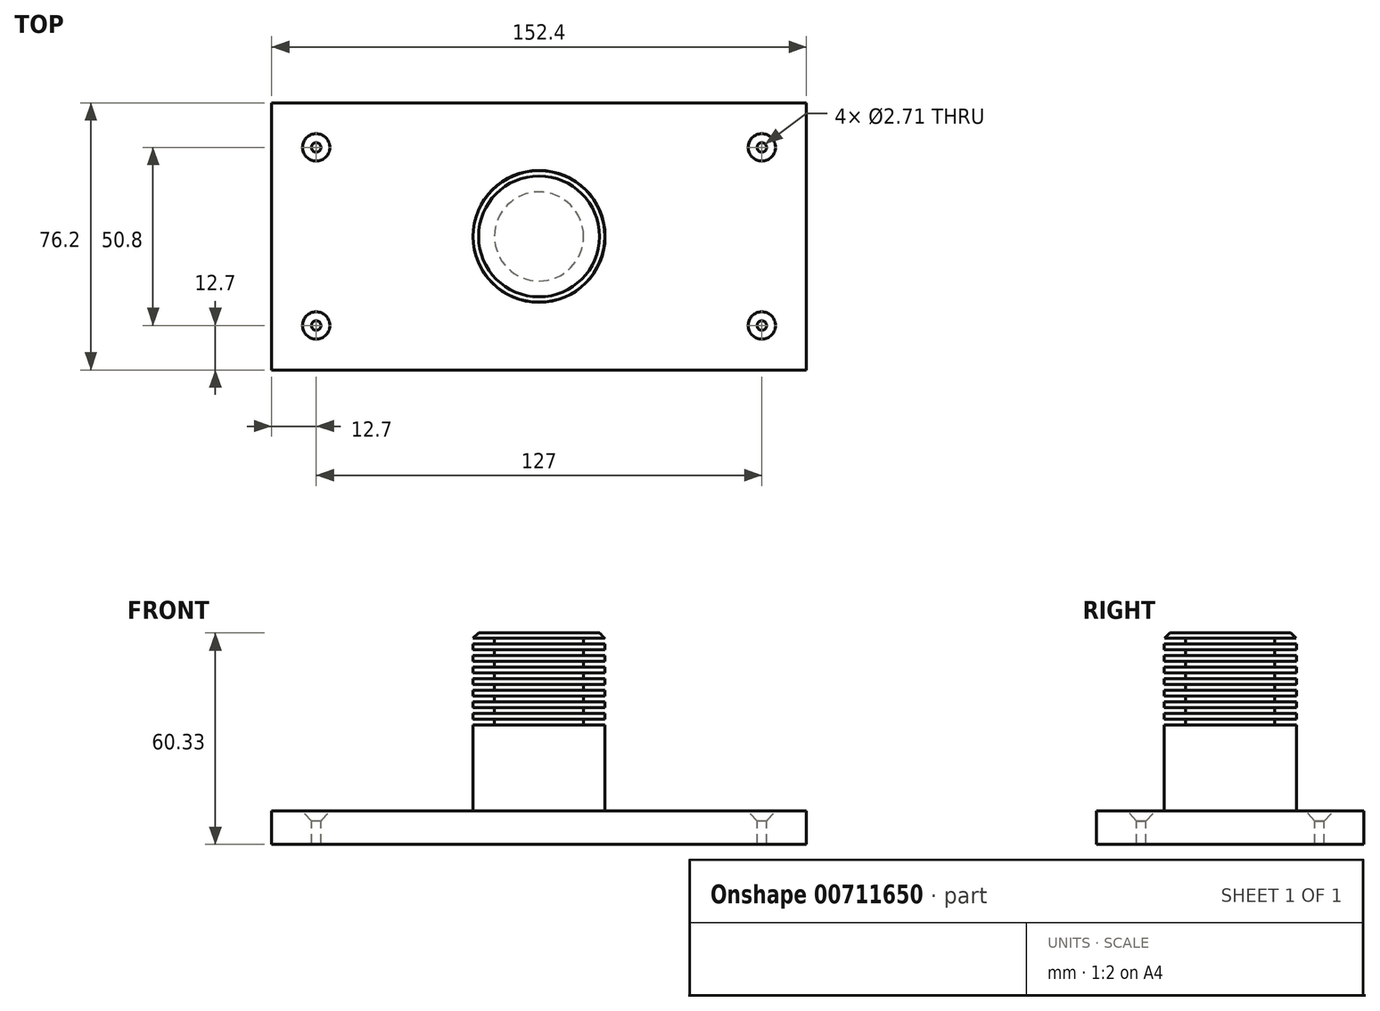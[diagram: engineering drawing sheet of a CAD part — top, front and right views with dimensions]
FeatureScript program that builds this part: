
annotation { "Feature Type Name" : "Feature", "Feature Type Description" : "" }
export const myFeature = defineFeature(function(context is Context, id is Id, definition is map)
    precondition{}
    {
        {
            var Q0;
            Q0=qCreatedBy(makeId("Top.planeOp"),FACE);
            var sketch = newSketch(context, id + "F0", { "sketchPlane" : qUnion([Q0])});
            skLineSegment(sketch, "E0.bottom", {"start": v(-76.2, 38.1) * mm, "end": v(76.2, 38.1) * mm});
            skLineSegment(sketch, "E0.top", {"start": v(-76.2, -38.1) * mm, "end": v(76.2, -38.1) * mm});
            skLineSegment(sketch, "E0.left", {"start": v(-76.2, 38.1) * mm, "end": v(-76.2, -38.1) * mm});
            skLineSegment(sketch, "E0.right", {"start": v(76.2, 38.1) * mm, "end": v(76.2, -38.1) * mm});
            skPoint(sketch, "E0.middle", {"position": v(0, 0) * mm});
            skSolve(sketch);
        }
        {
            var Q0;
            Q0=makeQuery(id+"F0.imprint","IMPRINT",FACE,{"disambiguationData":[TD([[makeQuery(id+"F0.imprint","IMPRINT",EDGE,{"derivedFrom":sQuery(id+"F0.wireOp",EDGE,"E0.bottom")}),-1.0]])]});
            extrude(context, id + "F1", {"entities" : qUnion([Q0]), "depth" : 9.52 * mm, "offsetDistance" : 25.4 * mm});
        }
        {
            var Q0;
            Q0=makeQuery(id+"F1.opExtrude","CAP_FACE",FACE,{"disambiguationData":[OSD([sQuery(id+"F0.wireOp",EDGE,"E0.bottom"),sQuery(id+"F0.wireOp",EDGE,"E0.top"),sQuery(id+"F0.wireOp",EDGE,"E0.left"),sQuery(id+"F0.wireOp",EDGE,"E0.right")])],"isStart":false});
            var sketch = newSketch(context, id + "F2", { "sketchPlane" : qUnion([Q0])});
            skPoint(sketch, "E1", {"position": v(-63.5, 25.4) * mm});
            skPoint(sketch, "E2", {"position": v(63.5, 25.4) * mm});
            skPoint(sketch, "E3.MirrorP", {"position": v(-63.5, -25.4) * mm});
            skPoint(sketch, "E4.MirrorP", {"position": v(63.5, -25.4) * mm});
            skSolve(sketch);
        }
        {
            var Q0;
            Q0=sQuery(id+"F2.wireOp",VERTEX,"E1");
            var Q1;
            Q1=sQuery(id+"F2.wireOp",VERTEX,"E2");
            var Q2;
            Q2=sQuery(id+"F2.wireOp",VERTEX,"E3.MirrorP");
            var Q3;
            Q3=sQuery(id+"F2.wireOp",VERTEX,"E4.MirrorP");
            var Q4;
            Q4=makeQuery(id+"F1.opExtrude","SWEPT_BODY",BODY,{"disambiguationData":[OSD([sQuery(id+"F0.wireOp",EDGE,"E0.bottom"),sQuery(id+"F0.wireOp",EDGE,"E0.top"),sQuery(id+"F0.wireOp",EDGE,"E0.left"),sQuery(id+"F0.wireOp",EDGE,"E0.right")])]});
            hole(context, id + "F3", {"style" : HoleStyle.C_SINK, "endStyle" : HoleEndStyle.THROUGH, "standardTappedOrClearance" : lookupTablePath({ "standard" : "ANSI", "engagement" : "75%", "pitch" : "32 tpi", "size" : "#6", "type" : "Tapped" }), "standardBlindInLast" : lookupTablePath({ "standard" : "ANSI", "engagement" : "75%", "pitch" : "32 tpi", "size" : "#6", "type" : "Tapped" }), "holeDiameter" : 2.7 * mm, "cSinkDiameter" : 7.8 * mm, "cSinkAngle" : 82 * degree, "majorDiameter" : 3.5 * mm, "showTappedDepth" : true, "isTappedThrough" : true, "tappedDepth" : 12.7 * mm, "tapClearance" : 3, "startFromSketch" : true, "locations" : qUnion([Q0, Q1, Q2, Q3]), "scope" : qUnion([Q4])});
        }
        {
            var Q0;
            Q0=makeQuery(id+"F1.opExtrude","CAP_FACE",FACE,{"disambiguationData":[OSD([sQuery(id+"F0.wireOp",EDGE,"E0.bottom"),sQuery(id+"F0.wireOp",EDGE,"E0.top"),sQuery(id+"F0.wireOp",EDGE,"E0.left"),sQuery(id+"F0.wireOp",EDGE,"E0.right")])],"isStart":false});
            var sketch = newSketch(context, id + "F4", { "sketchPlane" : qUnion([Q0])});
            skCircle(sketch, "E5", {"center": v(0, 0) * mm, "radius": 18.82 * mm});
            skSolve(sketch);
        }
        {
            var Q0;
            Q0 = qSketchRegion(id + "F4", true);
            extrude(context, id + "F5", {"entities" : qUnion([Q0]), "operationType" : NewBodyOperationType.ADD, "depth" : 50.8 * mm, "offsetDistance" : 25.4 * mm});
        }
        {
            var Q0;
            Q0=qCreatedBy(makeId("Front.planeOp"),FACE);
            var sketch = newSketch(context, id + "F6", { "sketchPlane" : qUnion([Q0])});
            skLineSegment(sketch, "E6.bottom", {"start": v(27.04, 35.68) * mm, "end": v(12.7, 35.68) * mm});
            skLineSegment(sketch, "E6.top", {"start": v(27.04, 34.1) * mm, "end": v(12.7, 34.1) * mm});
            skLineSegment(sketch, "E6.left", {"start": v(27.04, 35.68) * mm, "end": v(27.04, 34.1) * mm});
            skLineSegment(sketch, "E6.right", {"start": v(12.7, 35.68) * mm, "end": v(12.7, 34.1) * mm});
            skLineSegment(sketch, "E7.0.1.0", {"start": v(27.04, 37.4) * mm, "end": v(12.7, 37.4) * mm});
            skLineSegment(sketch, "E7.0.1.1", {"start": v(27.04, 38.98) * mm, "end": v(12.7, 38.98) * mm});
            skLineSegment(sketch, "E7.0.1.2", {"start": v(12.7, 38.98) * mm, "end": v(12.7, 37.4) * mm});
            skLineSegment(sketch, "E7.0.1.3", {"start": v(27.04, 38.98) * mm, "end": v(27.04, 37.4) * mm});
            skLineSegment(sketch, "E7.0.2.0", {"start": v(27.04, 40.7) * mm, "end": v(12.7, 40.7) * mm});
            skLineSegment(sketch, "E7.0.2.1", {"start": v(27.04, 42.29) * mm, "end": v(12.7, 42.29) * mm});
            skLineSegment(sketch, "E7.0.2.2", {"start": v(12.7, 42.29) * mm, "end": v(12.7, 40.7) * mm});
            skLineSegment(sketch, "E7.0.2.3", {"start": v(27.04, 42.29) * mm, "end": v(27.04, 40.7) * mm});
            skLineSegment(sketch, "E7.0.3.0", {"start": v(27.04, 44) * mm, "end": v(12.7, 44) * mm});
            skLineSegment(sketch, "E7.0.3.1", {"start": v(27.04, 45.59) * mm, "end": v(12.7, 45.59) * mm});
            skLineSegment(sketch, "E7.0.3.2", {"start": v(12.7, 45.59) * mm, "end": v(12.7, 44) * mm});
            skLineSegment(sketch, "E7.0.3.3", {"start": v(27.04, 45.59) * mm, "end": v(27.04, 44) * mm});
            skLineSegment(sketch, "E7.0.4.0", {"start": v(27.04, 47.3) * mm, "end": v(12.7, 47.3) * mm});
            skLineSegment(sketch, "E7.0.4.1", {"start": v(27.04, 48.89) * mm, "end": v(12.7, 48.89) * mm});
            skLineSegment(sketch, "E7.0.4.2", {"start": v(12.7, 48.89) * mm, "end": v(12.7, 47.3) * mm});
            skLineSegment(sketch, "E7.0.4.3", {"start": v(27.04, 48.89) * mm, "end": v(27.04, 47.3) * mm});
            skLineSegment(sketch, "E7.0.5.0", {"start": v(27.04, 50.6) * mm, "end": v(12.7, 50.6) * mm});
            skLineSegment(sketch, "E7.0.5.1", {"start": v(27.04, 52.2) * mm, "end": v(12.7, 52.2) * mm});
            skLineSegment(sketch, "E7.0.5.2", {"start": v(12.7, 52.2) * mm, "end": v(12.7, 50.6) * mm});
            skLineSegment(sketch, "E7.0.5.3", {"start": v(27.04, 52.2) * mm, "end": v(27.04, 50.6) * mm});
            skLineSegment(sketch, "E7.0.6.0", {"start": v(27.04, 53.9) * mm, "end": v(12.7, 53.9) * mm});
            skLineSegment(sketch, "E7.0.6.1", {"start": v(27.04, 55.5) * mm, "end": v(12.7, 55.5) * mm});
            skLineSegment(sketch, "E7.0.6.2", {"start": v(12.7, 55.5) * mm, "end": v(12.7, 53.9) * mm});
            skLineSegment(sketch, "E7.0.6.3", {"start": v(27.04, 55.5) * mm, "end": v(27.04, 53.9) * mm});
            skLineSegment(sketch, "E7.0.7.0", {"start": v(27.04, 57.2) * mm, "end": v(12.7, 57.2) * mm});
            skLineSegment(sketch, "E7.0.7.1", {"start": v(27.04, 58.8) * mm, "end": v(12.7, 58.8) * mm});
            skLineSegment(sketch, "E7.0.7.2", {"start": v(12.7, 58.8) * mm, "end": v(12.7, 57.2) * mm});
            skLineSegment(sketch, "E7.0.7.3", {"start": v(27.04, 58.8) * mm, "end": v(27.04, 57.2) * mm});
            skLineSegment(sketch, "E7.direction1", {"start": v(12.7, 34.1) * mm, "end": v(38.1, 34.1) * mm, "construction": true});
            skLineSegment(sketch, "E7.direction2", {"start": v(12.7, 34.1) * mm, "end": v(12.7, 37.4) * mm, "construction": true});
            skSolve(sketch);
        }
        {
            var Q0;
            Q0 = qSketchRegion(id + "F6", true);
            var Q1;
            Q1=makeQuery(id+"F5.opExtrude","SWEPT_FACE",FACE,{"disambiguationData":[OSD([sQuery(id+"F4.wireOp",EDGE,"E5")])]});
            revolve(context, id + "F7", {"operationType" : NewBodyOperationType.REMOVE, "surfaceOperationType" : NewSurfaceOperationType.NEW, "entities" : qUnion([Q0]), "axis" : qUnion([Q1]), "revolveType" : RevolveType.FULL, "oppositeDirection" : true});
        }
        {
            var Q0;
            Q0=makeQuery(id+"F5.opExtrude","CAP_FACE",FACE,{"disambiguationData":[OSD([sQuery(id+"F4.wireOp",EDGE,"E5")])],"isStart":false});
            var Q1;
            Q1=makeQuery(id+"F5.opExtrude","CAP_EDGE",EDGE,{"disambiguationData":[OSD([sQuery(id+"F4.wireOp",EDGE,"E5")])],"isStart":true});
            chamfer(context, id + "F8", {"entities" : qUnion([Q0, Q1]), "width" : 1.59 * mm, "tangentPropagation" : true});
        }
    });
